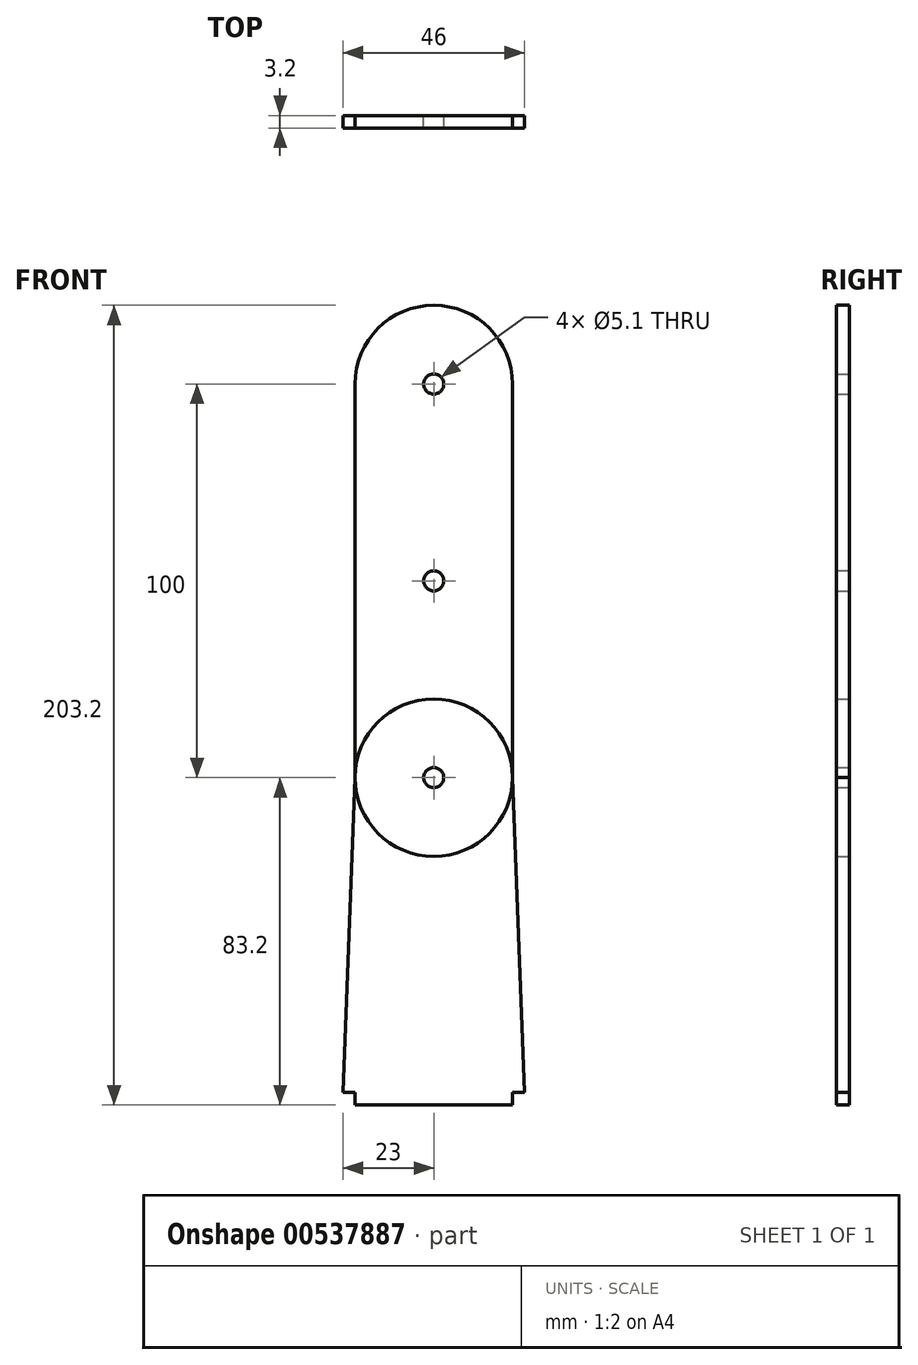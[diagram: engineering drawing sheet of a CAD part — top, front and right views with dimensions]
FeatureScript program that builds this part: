
annotation { "Feature Type Name" : "Feature", "Feature Type Description" : "" }
export const myFeature = defineFeature(function(context is Context, id is Id, definition is map)
    precondition{}
    {
        {
            var Q0;
            Q0=qCreatedBy(makeId("Front.planeOp"),FACE);
            var sketch = newSketch(context, id + "F0", { "sketchPlane" : qUnion([Q0])});
            skLineSegment(sketch, "E0.bottom", {"start": v(-20, -16.8) * mm, "end": v(20, -16.8) * mm});
            skLineSegment(sketch, "E0.top", {"start": v(-20, -20) * mm, "end": v(20, -20) * mm});
            skLineSegment(sketch, "E0.left", {"start": v(-20, -16.8) * mm, "end": v(-20, -20) * mm});
            skLineSegment(sketch, "E0.right", {"start": v(20, -16.8) * mm, "end": v(20, -20) * mm});
            skLineSegment(sketch, "E1", {"start": v(-20, -16.8) * mm, "end": v(-23, -16.8) * mm});
            skLineSegment(sketch, "E2", {"start": v(20, -16.8) * mm, "end": v(23, -16.8) * mm});
            skLineSegment(sketch, "E3", {"start": v(-23, -16.8) * mm, "end": v(-20, 63.2) * mm});
            skLineSegment(sketch, "E4", {"start": v(20, 63.2) * mm, "end": v(23, -16.8) * mm});
            skCircle(sketch, "E5", {"center": v(0, 63.2) * mm, "radius": 2.55 * mm});
            skPoint(sketch, "E6", {"position": v(0, -16.8) * mm});
            skArc(sketch, "E7", {"start": v(20, 63.2) * mm, "mid": v(0, 83.2) * mm, "end": v(-20, 63.2) * mm});
            skLineSegment(sketch, "E8", {"start": v(-20, 63.2) * mm, "end": v(20, 63.2) * mm, "construction": true});
            skSolve(sketch);
        }
        {
            var Q0;
            Q0=makeQuery(id+"F0.imprint","IMPRINT",FACE,{"disambiguationData":[TD([[makeQuery(id+"F0.imprint","IMPRINT",EDGE,{"derivedFrom":sQuery(id+"F0.wireOp",EDGE,"E0.bottom")}),1.0]])]});
            var Q1;
            Q1=makeQuery(id+"F0.imprint","IMPRINT",FACE,{"disambiguationData":[TD([[makeQuery(id+"F0.imprint","IMPRINT",EDGE,{"derivedFrom":sQuery(id+"F0.wireOp",EDGE,"E0.bottom")}),-1.0]])]});
            extrude(context, id + "F1", {"entities" : qUnion([Q0, Q1]), "depth" : 3.2 * mm, "offsetDistance" : 25 * mm});
        }
        {
            var Q0;
            Q0=qCreatedBy(makeId("Front.planeOp"),FACE);
            var sketch = newSketch(context, id + "F2", { "sketchPlane" : qUnion([Q0])});
            skCircle(sketch, "E9.0", {"center": v(0, 63.2) * mm, "radius": 2.55 * mm});
            skArc(sketch, "E10", {"start": v(-20, 63.2) * mm, "mid": v(0, 43.2) * mm, "end": v(20, 63.2) * mm});
            skLineSegment(sketch, "E11", {"start": v(-68.03, 63.2) * mm, "end": v(-20, 63.2) * mm, "construction": true});
            skPoint(sketch, "E12", {"position": v(-20, 63.2) * mm});
            skPoint(sketch, "E13", {"position": v(20, 63.2) * mm});
            skLineSegment(sketch, "E14.bottom", {"start": v(-20, 63.2) * mm, "end": v(20, 63.2) * mm});
            skLineSegment(sketch, "E14.left", {"start": v(-20, 63.2) * mm, "end": v(-20, 163.2) * mm});
            skLineSegment(sketch, "E14.right", {"start": v(20, 63.2) * mm, "end": v(20, 163.2) * mm});
            skPoint(sketch, "E15", {"position": v(0, 163.2) * mm});
            skArc(sketch, "E16", {"start": v(20, 163.2) * mm, "mid": v(0, 183.2) * mm, "end": v(-20, 163.2) * mm});
            skLineSegment(sketch, "E17.trimOffspring", {"start": v(-2.55, 63.2) * mm, "end": v(2.55, 63.2) * mm, "construction": true});
            skLineSegment(sketch, "E18.trimOffspring", {"start": v(20, 63.2) * mm, "end": v(70.85, 63.2) * mm, "construction": true});
            skCircle(sketch, "E19", {"center": v(0, 163.2) * mm, "radius": 2.55 * mm});
            skPoint(sketch, "E20", {"position": v(-20, 113.2) * mm});
            skPoint(sketch, "E21", {"position": v(20, 113.2) * mm});
            skCircle(sketch, "E22", {"center": v(0, 113.2) * mm, "radius": 2.55 * mm});
            skSolve(sketch);
        }
        {
            var Q0;
            Q0=qSketchRegion(id+"F2",true);
            extrude(context, id + "F3", {"entities" : qUnion([Q0]), "depth" : 3.2 * mm, "offsetDistance" : 25 * mm});
        }
    });
